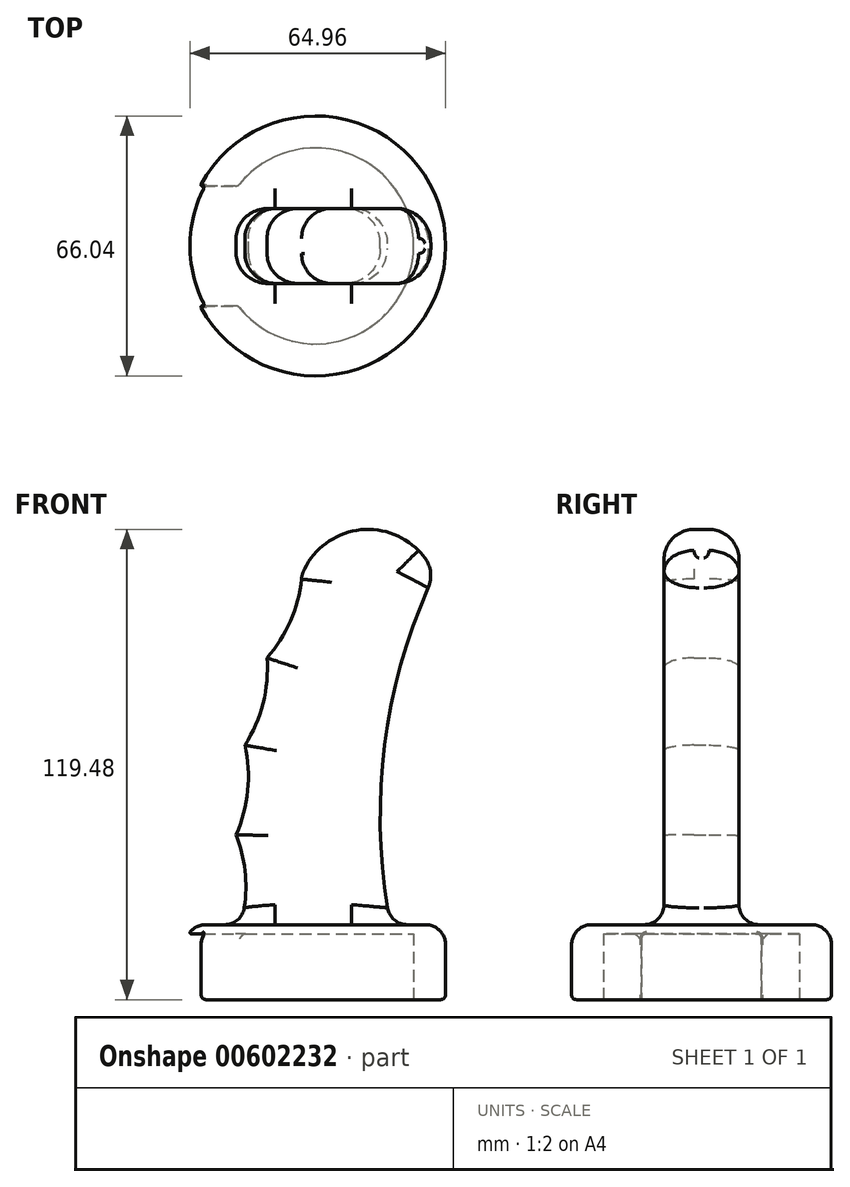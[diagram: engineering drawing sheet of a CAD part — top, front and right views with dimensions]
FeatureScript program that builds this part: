
annotation { "Feature Type Name" : "Feature", "Feature Type Description" : "" }
export const myFeature = defineFeature(function(context is Context, id is Id, definition is map)
    precondition{}
    {
        {
            var Q0;
            Q0=qCreatedBy(makeId("Front.planeOp"),FACE);
            var sketch = newSketch(context, id + "F0", { "sketchPlane" : qUnion([Q0])});
            skArc(sketch, "E0", {"start": v(30.11, 88.9) * mm, "mid": v(17.5, 45.33) * mm, "end": v(19.05, 0) * mm});
            skArc(sketch, "E1", {"start": v(30.11, 88.9) * mm, "mid": v(13.3, 100.43) * mm, "end": v(-3.5, 88.9) * mm});
            skLineSegment(sketch, "E2", {"start": v(-19.05, 0) * mm, "end": v(0, 0) * mm});
            skLineSegment(sketch, "E3", {"start": v(0, 0) * mm, "end": v(19.05, 0) * mm});
            skArc(sketch, "E4", {"start": v(-19.05, 0) * mm, "mid": v(-17.78, 11.52) * mm, "end": v(-20.21, 22.85) * mm});
            skArc(sketch, "E5", {"start": v(-20.21, 22.85) * mm, "mid": v(-17.24, 34.05) * mm, "end": v(-17.96, 45.62) * mm});
            skArc(sketch, "E6", {"start": v(-17.96, 45.62) * mm, "mid": v(-13.36, 56.26) * mm, "end": v(-12.35, 67.8) * mm});
            skArc(sketch, "E7", {"start": v(-12.35, 67.8) * mm, "mid": v(-6.2, 77.63) * mm, "end": v(-3.5, 88.9) * mm});
            skLineSegment(sketch, "E8", {"start": v(-19.05, 0) * mm, "end": v(-20.21, 22.85) * mm, "construction": true});
            skLineSegment(sketch, "E9", {"start": v(-17.96, 45.62) * mm, "end": v(-12.35, 67.8) * mm, "construction": true});
            skLineSegment(sketch, "E10", {"start": v(-17.96, 45.62) * mm, "end": v(-20.21, 22.85) * mm, "construction": true});
            skLineSegment(sketch, "E11", {"start": v(-12.35, 67.8) * mm, "end": v(-3.5, 88.9) * mm, "construction": true});
            skSolve(sketch);
        }
        {
            var Q0;
            Q0 = qSketchRegion(id + "F0", true);
            extrude(context, id + "F1", {"entities" : qUnion([Q0]), "endBound" : BoundingType.SYMMETRIC, "depth" : 19.05 * mm, "offsetDistance" : 25.4 * mm});
        }
        {
            var Q0;
            Q0=makeQuery(id+"F1.opExtrude","CAP_EDGE",EDGE,{"disambiguationData":[OSD([sQuery(id+"F0.wireOp",EDGE,"E4")])],"isStart":false});
            var Q1;
            Q1=makeQuery(id+"F1.opExtrude","CAP_EDGE",EDGE,{"disambiguationData":[OSD([sQuery(id+"F0.wireOp",EDGE,"E5")])],"isStart":false});
            var Q2;
            Q2=makeQuery(id+"F1.opExtrude","CAP_EDGE",EDGE,{"disambiguationData":[OSD([sQuery(id+"F0.wireOp",EDGE,"E6")])],"isStart":false});
            var Q3;
            Q3=makeQuery(id+"F1.opExtrude","CAP_EDGE",EDGE,{"disambiguationData":[OSD([sQuery(id+"F0.wireOp",EDGE,"E7")])],"isStart":false});
            var Q4;
            Q4=makeQuery(id+"F1.opExtrude","CAP_EDGE",EDGE,{"disambiguationData":[OSD([sQuery(id+"F0.wireOp",EDGE,"E7")])],"isStart":true});
            var Q5;
            Q5=makeQuery(id+"F1.opExtrude","CAP_EDGE",EDGE,{"disambiguationData":[OSD([sQuery(id+"F0.wireOp",EDGE,"E6")])],"isStart":true});
            var Q6;
            Q6=makeQuery(id+"F1.opExtrude","CAP_EDGE",EDGE,{"disambiguationData":[OSD([sQuery(id+"F0.wireOp",EDGE,"E5")])],"isStart":true});
            var Q7;
            Q7=makeQuery(id+"F1.opExtrude","CAP_EDGE",EDGE,{"disambiguationData":[OSD([sQuery(id+"F0.wireOp",EDGE,"E4")])],"isStart":true});
            fillet(context, id + "F2", {"entities" : qUnion([Q0, Q1, Q2, Q3, Q4, Q5, Q6, Q7]), "radius" : 7.62 * mm, "tangentPropagation" : true, "allowEdgeOverflow" : false});
        }
        {
            var Q0;
            Q0=makeQuery(id+"F1.opExtrude","CAP_EDGE",EDGE,{"disambiguationData":[OSD([sQuery(id+"F0.wireOp",EDGE,"E0")])],"isStart":false});
            var Q1;
            Q1=makeQuery(id+"F1.opExtrude","CAP_EDGE",EDGE,{"disambiguationData":[OSD([sQuery(id+"F0.wireOp",EDGE,"E0")])],"isStart":true});
            fillet(context, id + "F3", {"entities" : qUnion([Q0, Q1]), "radius" : 8.9 * mm, "tangentPropagation" : true, "allowEdgeOverflow" : false});
        }
        {
            var Q0;
            Q0=makeQuery(id+"F1.opExtrude","CAP_EDGE",EDGE,{"disambiguationData":[OSD([sQuery(id+"F0.wireOp",EDGE,"E1")])],"isStart":false});
            fillet(context, id + "F4", {"entities" : qUnion([Q0]), "radius" : 7.62 * mm, "tangentPropagation" : true, "allowEdgeOverflow" : false});
        }
        {
            var Q0;
            Q0=makeQuery(id+"F1.opExtrude","SWEPT_FACE",FACE,{"disambiguationData":[OSD([sQuery(id+"F0.wireOp",EDGE,"E2"),sQuery(id+"F0.wireOp",EDGE,"E3")])]});
            var sketch = newSketch(context, id + "F5", { "sketchPlane" : qUnion([Q0])});
            skCircle(sketch, "E12", {"center": v(0, 0) * mm, "radius": 33.02 * mm});
            skSolve(sketch);
        }
        {
            var Q0;
            Q0 = qSketchRegion(id + "F5", true);
            extrude(context, id + "F6", {"entities" : qUnion([Q0]), "operationType" : NewBodyOperationType.ADD, "depth" : 19.05 * mm, "offsetDistance" : 25.4 * mm});
        }
        {
            var Q0;
            Q0=makeQuery(id+"F6.opExtrude","CAP_FACE",FACE,{"disambiguationData":[OSD([sQuery(id+"F5.wireOp",EDGE,"E12")])],"isStart":true});
            fillet(context, id + "F7", {"entities" : qUnion([Q0]), "radius" : 5.08 * mm, "tangentPropagation" : true, "allowEdgeOverflow" : false});
        }
        {
            var Q0;
            Q0=makeQuery(id+"F6.opExtrude","CAP_FACE",FACE,{"disambiguationData":[OSD([sQuery(id+"F5.wireOp",EDGE,"E12")])],"isStart":false});
            var sketch = newSketch(context, id + "F8", { "sketchPlane" : qUnion([Q0])});
            skCircle(sketch, "E13", {"center": v(0, 0) * mm, "radius": 24.9 * mm});
            skSolve(sketch);
        }
        {
            var Q0;
            Q0 = qSketchRegion(id + "F8", true);
            extrude(context, id + "F9", {"entities" : qUnion([Q0]), "operationType" : NewBodyOperationType.REMOVE, "oppositeDirection" : true, "depth" : 16.76 * mm, "offsetDistance" : 25.4 * mm});
        }
        {
            var Q0;
            Q0=makeQuery(id+"F6.opExtrude","CAP_FACE",FACE,{"disambiguationData":[OSD([sQuery(id+"F5.wireOp",EDGE,"E12")])],"isStart":false});
            var sketch = newSketch(context, id + "F10", { "sketchPlane" : qUnion([Q0])});
            skLineSegment(sketch, "E14.bottom", {"start": v(-14.08, 15.24) * mm, "end": v(-108.33, 15.24) * mm});
            skLineSegment(sketch, "E14.top", {"start": v(-14.08, -15.24) * mm, "end": v(-108.33, -15.24) * mm});
            skLineSegment(sketch, "E14.left", {"start": v(-14.08, 15.24) * mm, "end": v(-14.08, -15.24) * mm});
            skLineSegment(sketch, "E14.right", {"start": v(-108.33, 15.24) * mm, "end": v(-108.33, -15.24) * mm});
            skPoint(sketch, "E14.middle", {"position": v(-61.2, 0) * mm});
            skSolve(sketch);
        }
        {
            var Q0;
            Q0 = qSketchRegion(id + "F10", true);
            var Q1;
            Q1=makeQuery(id+"F9.boolean.opBoolean","COPY",FACE,{"derivedFrom":makeQuery(id+"F9.opExtrude","CAP_FACE",FACE,{"disambiguationData":[OSD([sQuery(id+"F8.wireOp",EDGE,"E13")])],"isStart":false})});
            extrude(context, id + "F11", {"entities" : qUnion([Q0]), "operationType" : NewBodyOperationType.REMOVE, "endBound" : BoundingType.UP_TO_SURFACE, "oppositeDirection" : true, "depth" : 25.4 * mm, "endBoundEntityFace" : qUnion([Q1]), "offsetDistance" : 25.4 * mm});
        }
        {
            var Q0;
            Q0=makeQuery(id+"F11.boolean.opBoolean","COPY",EDGE,{"derivedFrom":makeQuery(id+"F11.opExtrude","CAP_EDGE",EDGE,{"disambiguationData":[OSD([sQuery(id+"F10.wireOp",EDGE,"E14.bottom")])],"isStart":false})});
            var Q1;
            Q1=makeQuery(id+"F11.boolean.opBoolean","INTERSECT",EDGE,{"derivedFrom":[makeQuery(id+"F9.boolean.opBoolean","COPY",FACE,{"derivedFrom":makeQuery(id+"F9.opExtrude","SWEPT_FACE",FACE,{"disambiguationData":[OSD([sQuery(id+"F8.wireOp",EDGE,"E13")])]})}),makeQuery(id+"F11.opExtrude","SWEPT_FACE",FACE,{"disambiguationData":[OSD([sQuery(id+"F10.wireOp",EDGE,"E14.bottom")])]})]});
            var Q2;
            Q2=makeQuery(id+"F11.boolean.opBoolean","COPY",EDGE,{"derivedFrom":makeQuery(id+"F11.opExtrude","CAP_EDGE",EDGE,{"disambiguationData":[OSD([sQuery(id+"F10.wireOp",EDGE,"E14.bottom")])],"isStart":true})});
            var Q3;
            Q3=makeQuery(id+"F11.boolean.opBoolean","COPY",EDGE,{"derivedFrom":makeQuery(id+"F11.opExtrude","CAP_EDGE",EDGE,{"disambiguationData":[OSD([sQuery(id+"F10.wireOp",EDGE,"E14.top")])],"isStart":false})});
            var Q4;
            Q4=makeQuery(id+"F11.boolean.opBoolean","INTERSECT",EDGE,{"derivedFrom":[makeQuery(id+"F9.boolean.opBoolean","COPY",FACE,{"derivedFrom":makeQuery(id+"F9.opExtrude","SWEPT_FACE",FACE,{"disambiguationData":[OSD([sQuery(id+"F8.wireOp",EDGE,"E13")])]})}),makeQuery(id+"F11.opExtrude","SWEPT_FACE",FACE,{"disambiguationData":[OSD([sQuery(id+"F10.wireOp",EDGE,"E14.top")])]})]});
            var Q5;
            Q5=makeQuery(id+"F11.boolean.opBoolean","COPY",EDGE,{"derivedFrom":makeQuery(id+"F11.opExtrude","CAP_EDGE",EDGE,{"disambiguationData":[OSD([sQuery(id+"F10.wireOp",EDGE,"E14.top")])],"isStart":true})});
            var Q6;
            Q6=makeQuery(id+"F9.boolean.opBoolean","COPY",EDGE,{"derivedFrom":makeQuery(id+"F9.opExtrude","CAP_EDGE",EDGE,{"disambiguationData":[OSD([sQuery(id+"F8.wireOp",EDGE,"E13")])],"isStart":true})});
            var Q7;
            Q7=makeQuery(id+"F6.opExtrude","CAP_EDGE",EDGE,{"disambiguationData":[OSD([sQuery(id+"F5.wireOp",EDGE,"E12")])],"isStart":false});
            fillet(context, id + "F12", {"entities" : qUnion([Q0, Q1, Q2, Q3, Q4, Q5, Q6, Q7]), "radius" : 1.27 * mm, "tangentPropagation" : true, "allowEdgeOverflow" : false});
        }
        {
            var Q0;
            Q0=makeQuery(id+"F11.boolean.opBoolean","INTERSECT",EDGE,{"derivedFrom":[makeQuery(id+"F6.opExtrude","SWEPT_FACE",FACE,{"disambiguationData":[OSD([sQuery(id+"F5.wireOp",EDGE,"E12")])]}),makeQuery(id+"F11.opExtrude","SWEPT_FACE",FACE,{"disambiguationData":[OSD([sQuery(id+"F10.wireOp",EDGE,"E14.bottom")])]})]});
            var Q1;
            Q1=makeQuery(id+"F11.boolean.opBoolean","INTERSECT",EDGE,{"derivedFrom":[makeQuery(id+"F7.opFillet","BLEND_FACE",FACE,{"disambiguationData":[OSD([sQuery(id+"F5.wireOp",EDGE,"E12")])]}),makeQuery(id+"F11.opExtrude","SWEPT_FACE",FACE,{"disambiguationData":[OSD([sQuery(id+"F10.wireOp",EDGE,"E14.bottom")])]})]});
            var Q2;
            Q2=makeQuery(id+"F12.opFillet","BLEND_EDGE",EDGE,{"blendedFrom":[makeQuery(id+"F11.boolean.opBoolean","COPY",EDGE,{"derivedFrom":makeQuery(id+"F11.opExtrude","CAP_EDGE",EDGE,{"disambiguationData":[OSD([sQuery(id+"F10.wireOp",EDGE,"E14.bottom")])],"isStart":false})}),makeQuery(id+"F7.opFillet","BLEND_FACE",FACE,{"disambiguationData":[OSD([sQuery(id+"F5.wireOp",EDGE,"E12")])]})],"blendedInto":[makeQuery(id+"F7.opFillet","BLEND_FACE",FACE,{"disambiguationData":[OSD([sQuery(id+"F5.wireOp",EDGE,"E12")])]})]});
            var Q3;
            Q3=makeQuery(id+"F11.boolean.opBoolean","INTERSECT",EDGE,{"derivedFrom":[makeQuery(id+"F7.opFillet","BLEND_FACE",FACE,{"disambiguationData":[OSD([sQuery(id+"F5.wireOp",EDGE,"E12")])]}),makeQuery(id+"F11.opExtrude","CAP_FACE",FACE,{"disambiguationData":[OSD([sQuery(id+"F10.wireOp",EDGE,"E14.bottom"),sQuery(id+"F10.wireOp",EDGE,"E14.top"),sQuery(id+"F10.wireOp",EDGE,"E14.left"),sQuery(id+"F10.wireOp",EDGE,"E14.right")])],"isStart":false})]});
            var Q4;
            Q4=makeQuery(id+"F12.opFillet","BLEND_EDGE",EDGE,{"blendedFrom":[makeQuery(id+"F11.boolean.opBoolean","COPY",EDGE,{"derivedFrom":makeQuery(id+"F11.opExtrude","CAP_EDGE",EDGE,{"disambiguationData":[OSD([sQuery(id+"F10.wireOp",EDGE,"E14.top")])],"isStart":false})}),makeQuery(id+"F7.opFillet","BLEND_FACE",FACE,{"disambiguationData":[OSD([sQuery(id+"F5.wireOp",EDGE,"E12")])]})],"blendedInto":[makeQuery(id+"F7.opFillet","BLEND_FACE",FACE,{"disambiguationData":[OSD([sQuery(id+"F5.wireOp",EDGE,"E12")])]})]});
            var Q5;
            Q5=makeQuery(id+"F11.boolean.opBoolean","INTERSECT",EDGE,{"derivedFrom":[makeQuery(id+"F7.opFillet","BLEND_FACE",FACE,{"disambiguationData":[OSD([sQuery(id+"F5.wireOp",EDGE,"E12")])]}),makeQuery(id+"F11.opExtrude","SWEPT_FACE",FACE,{"disambiguationData":[OSD([sQuery(id+"F10.wireOp",EDGE,"E14.top")])]})]});
            var Q6;
            Q6=makeQuery(id+"F11.boolean.opBoolean","INTERSECT",EDGE,{"derivedFrom":[makeQuery(id+"F6.opExtrude","SWEPT_FACE",FACE,{"disambiguationData":[OSD([sQuery(id+"F5.wireOp",EDGE,"E12")])]}),makeQuery(id+"F11.opExtrude","SWEPT_FACE",FACE,{"disambiguationData":[OSD([sQuery(id+"F10.wireOp",EDGE,"E14.top")])]})]});
            fillet(context, id + "F13", {"entities" : qUnion([Q0, Q1, Q2, Q3, Q4, Q5, Q6]), "radius" : 0.25 * mm, "tangentPropagation" : true, "allowEdgeOverflow" : false});
        }
    });
